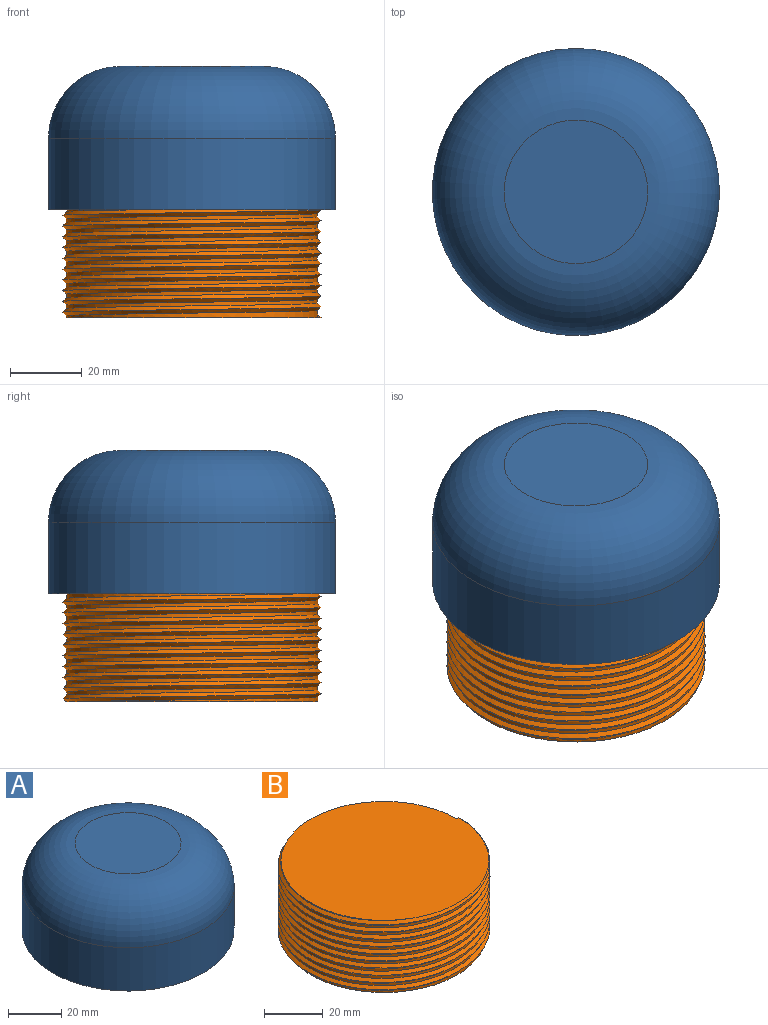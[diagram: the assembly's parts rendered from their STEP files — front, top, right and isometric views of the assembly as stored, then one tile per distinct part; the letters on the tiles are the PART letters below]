
ASSEMBLY  parts=2 mates=1
PART A: 12 faces, bbox 86.6x86.6x40 mm
  f0: cylinder r=40mm len=80mm, axis (0,0,-1), area 5026.5mm2, adj f2,f3
  f1: plane 40x40mm, normal (0,0,1), area 1256.6mm2, adj f3
  f2: plane 80x80mm, normal (0,0,-1), area 1178.1mm2, adj f0,f4
  f3: torus R=20mm, axis (0,0,1), area 6461.1mm2, adj f0,f1
  f4: cylinder r=35mm len=70mm, axis (0,0,-1), area 1697.9mm2, adj f2,f6,f8,f9,f10,f11
  f5: plane 40x40mm, normal (0,0,-1), area 1256.6mm2, adj f6
  f6: torus R=20mm, axis (0,0,1), area 4374.6mm2, adj f4,f5,f7
  f7: cylinder r=35mm len=3.91mm, axis (0,0,1), area 0.1mm2, adj f6,f9,f10
  f8: plane 2.05x1.05mm, normal (0,1,0), area 1.1mm2, adj f4,f10,f11
  f9: plane 2.05x1.05mm, normal (0,-1,0), area 1.1mm2, adj f4,f7,f10,f11
  f10: bspline ~83.25x72.1mm, area 1965.7mm2, adj f4,f7,f8,f9,f11
  f11: bspline ~83.25x72.1mm, area 1965.7mm2, adj f4,f8,f9,f10
PART B: 7 faces, bbox 72x83.1x32 mm
  f0: plane 1x1mm, normal (0,-1,0), area 0.5mm2, adj f3,f4,f6
  f1: bspline ~83.14x72mm, area 3096.3mm2, adj f2,f3,f4,f6
  f2: plane 1x1mm, normal (0,1,0), area 0.5mm2, adj f1,f4,f5
  f3: bspline ~83.14x72mm, area 3089.9mm2, adj f0,f1,f4,f5
  f4: cylinder r=35mm len=70mm, axis (0,0,-1), area 2234.3mm2, adj f0,f1,f2,f3,f5,f6
  f5: plane 71x70.26mm, normal (0,0,1), area 3885.4mm2, adj f2,f3,f4
  f6: plane 71x70.26mm, normal (0,0,-1), area 3885.4mm2, adj f0,f1,f4
PLACE A rot(axis=(0,0,1),13.4deg) t=(2.97,2.6,15.46)mm
PLACE B t=(2.97,2.6,-14.54)mm fixed
MATE cylindrical A.f0 <-> B.f4  axis (0,0,-1) through (2.97,2.6,15.46)mm
